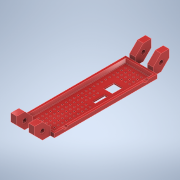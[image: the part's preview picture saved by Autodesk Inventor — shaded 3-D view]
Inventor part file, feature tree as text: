
AUTODESK INVENTOR PART (.ipt)
format: ipt  version: 2021 (Build 250183000, 183)  size: 374,272 bytes
history: native  units: in
note: dims shown in document units (in); Inventor stores cm internally (conversion verified against a paired STEP export)
features: other x4, extrude x4, hole x2, chamfer x1
ambient origin geometry x8: Origin, YZ Plane, XZ Plane, XY Plane, X Axis, Y Axis, Z Axis, Center Point
bodies: Solid1 (feature_tree)
feature tree (11):
  other  "Base Profile"
  extrude  "Base Extrusion"  Depth=0.7874in
  hole  "Fixing Holes"  [1 undecoded]
  other  "Cutouts"
  hole  "Vents"  [1 undecoded]
  extrude  "Cutouts Subtract"  Depth=0.1969in
  extrude  "Structure Subtract"  Depth=0.7874in
  chamfer  "Structure Clearance"  Distance=0.7874in
  extrude  "Standoff Clearance Subtract"  Depth=1.5748in TaperAngle=0.0deg
  other  "Structure"
  other  "Standoff Clearance"
note: 2 required parameter values undecoded (feature->parameter linkage not recoverable at this tier; creation-order binding heuristic only, values carry confidence <= 0.55)
